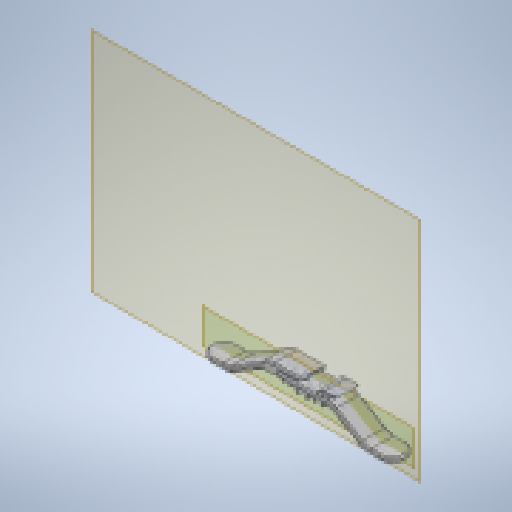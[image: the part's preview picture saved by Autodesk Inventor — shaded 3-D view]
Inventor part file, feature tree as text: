
AUTODESK INVENTOR PART (.ipt)
format: ipt  version: 2023 (Build 270158030, 158C)  size: 596,480 bytes
history: native  units: mm
features: fillet x7, chamfer x6, extrude x5, other x4, sketch x4, projected_geometry x3, plane x2, reference x2
ambient origin geometry x8: Origin, YZ Plane, XZ Plane, XY Plane, X Axis, Y Axis, Z Axis, Center Point
bodies: Body1 (feature_tree)
feature tree (33):
  other  "cable-hanger"
  extrude  "Extrusion1"  Depth=10.0mm TaperAngle=0.0deg
  fillet  "Fillet1"  Radius=7.5mm
  fillet  "Fillet2"  Radius=10.0mm
  chamfer  "Chamfer1"  Distance=1.0mm Angle=45.0deg
  plane  "Work Plane1"
  extrude  "Extrusion2"  Depth=10.0mm
  fillet  "Fillet3"  Radius=6.0mm
  fillet  "Fillet4"  Radius=4.0mm
  chamfer  "Chamfer2"  Distance=40.0mm
  plane  "Work Plane2"
  extrude  "Extrusion3"  Depth=8.0mm
  chamfer  "Chamfer3"  Distance=9.5mm
  chamfer  "Chamfer4"  Distance=1.2mm
  extrude  "Extrusion4"  Depth=8.0mm
  fillet  "Fillet5"  Radius=1.2mm
  fillet  "Fillet6"  Radius=2.5mm
  chamfer  "Chamfer5"  Distance=1.25mm
  extrude  "Extrusion5"  Depth=8.0mm
  fillet  "Fillet7"  Radius=1.5mm
  chamfer  "Chamfer6"  Distance=2.0mm
  sketch  "Sketch1"  dims[d0=3.0mm d1=3.0mm d2=3.0mm d3=17.0mm d4=-20.0mm d5=-12.0mm d6=20.0mm d7=114.0mm d8=20.0mm d9=-20.0mm d10=17.0mm d11=2.0mm d12=1.5mm d13=10.0mm d14=15.0mm d15=0.0mm d16=7.5mm d17=10.0mm d18=1.0mm d19=2.0mm d20=45.0deg]
  sketch  "Sketch2"  dims[d21=10.0mm d22=10.0mm d23=7.210321mm d24=7.25mm d25=3.3mm d26=4.0mm d27=5.0mm d28=1.2mm d29=1.2mm d30=1.2mm d31=2.5mm d32=1.25mm d33=1.65mm d34=0.825mm d35=2.0mm d36=1.0mm]
  projected_geometry  "Projected Loop1"
  projected_geometry  "Projected Loop2"
  projected_geometry  "Projected Loop3"
  reference  "Reference1"
  reference  "Reference2"
  sketch  "Sketch4"  dims[d37=10.0mm d38=10.0mm d39=7.210321mm d40=7.25mm d41=3.3mm d42=4.0mm d43=5.0mm d44=1.2mm d45=1.2mm d46=1.2mm d47=2.5mm d48=1.25mm d49=1.65mm d50=0.825mm d51=2.0mm d52=1.0mm d53=5.0mm d54=6.0mm d55=4.0mm]
  sketch  "Sketch5"  dims[d56=40.0mm d57=40.0mm d58=9.5mm d59=9.5mm d60=1.2mm d61=1.2mm d62=1.2mm d63=2.5mm d64=1.25mm d65=3.0mm d66=1.5mm d67=2.0mm d68=1.0mm d69=8.0mm d70=0.0mm d71=1.0mm d72=1.0mm d73=1.0mm d74=2.0mm d75=45.0deg d76=2.5mm d78=8.0mm d79=0.0mm d80=1.6mm d81=2.0mm d82=45.0deg d83=0.5mm d84=2.0mm d85=45.0deg d86=15.0mm d87=13.8mm d88=1.0mm d89=22.0mm d90=4.0mm d91=12.0mm d92=14.0mm d93=0.0mm d94=10.0mm d95=5.0mm d96=0.5mm d97=2.0mm d98=45.0deg d99=2.1mm d100=5.0mm d101=8.0mm d102=0.0mm d103=1.0mm d104=1.0mm d105=2.0mm d106=45.0deg]
  other  "<userpath>\Documents\0004-inventor\3D-CAD-main\cable-hanger\cable-hanger-hook.iam"
  other  "cable-hanger-hook.iam"
  other  "backplate-0:1"
